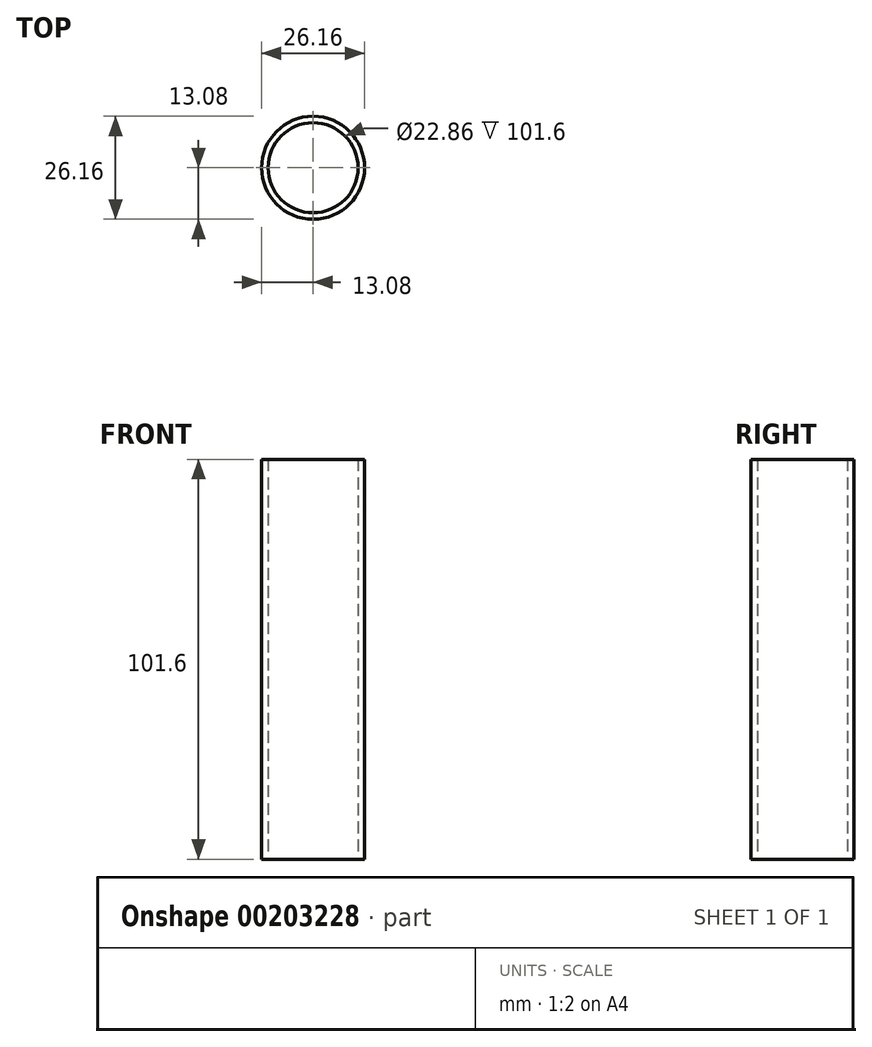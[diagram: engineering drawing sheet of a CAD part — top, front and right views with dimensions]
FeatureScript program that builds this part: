
annotation { "Feature Type Name" : "Feature", "Feature Type Description" : "" }
export const myFeature = defineFeature(function(context is Context, id is Id, definition is map)
    precondition{}
    {
        {
            var Q0;
            Q0=qCreatedBy(makeId("Top.planeOp"),FACE);
            var sketch = newSketch(context, id + "F0", { "sketchPlane" : qUnion([Q0])});
            skCircle(sketch, "E0", {"center": v(0, 0) * mm, "radius": 13.08 * mm});
            skCircle(sketch, "E1", {"center": v(0, 0) * mm, "radius": 11.43 * mm});
            skSolve(sketch);
        }
        {
            var Q0;
            Q0 = qSketchRegion(id + "F0", true);
            extrude(context, id + "F1", {"entities" : qUnion([Q0]), "depth" : 101.6 * mm});
        }
    });
